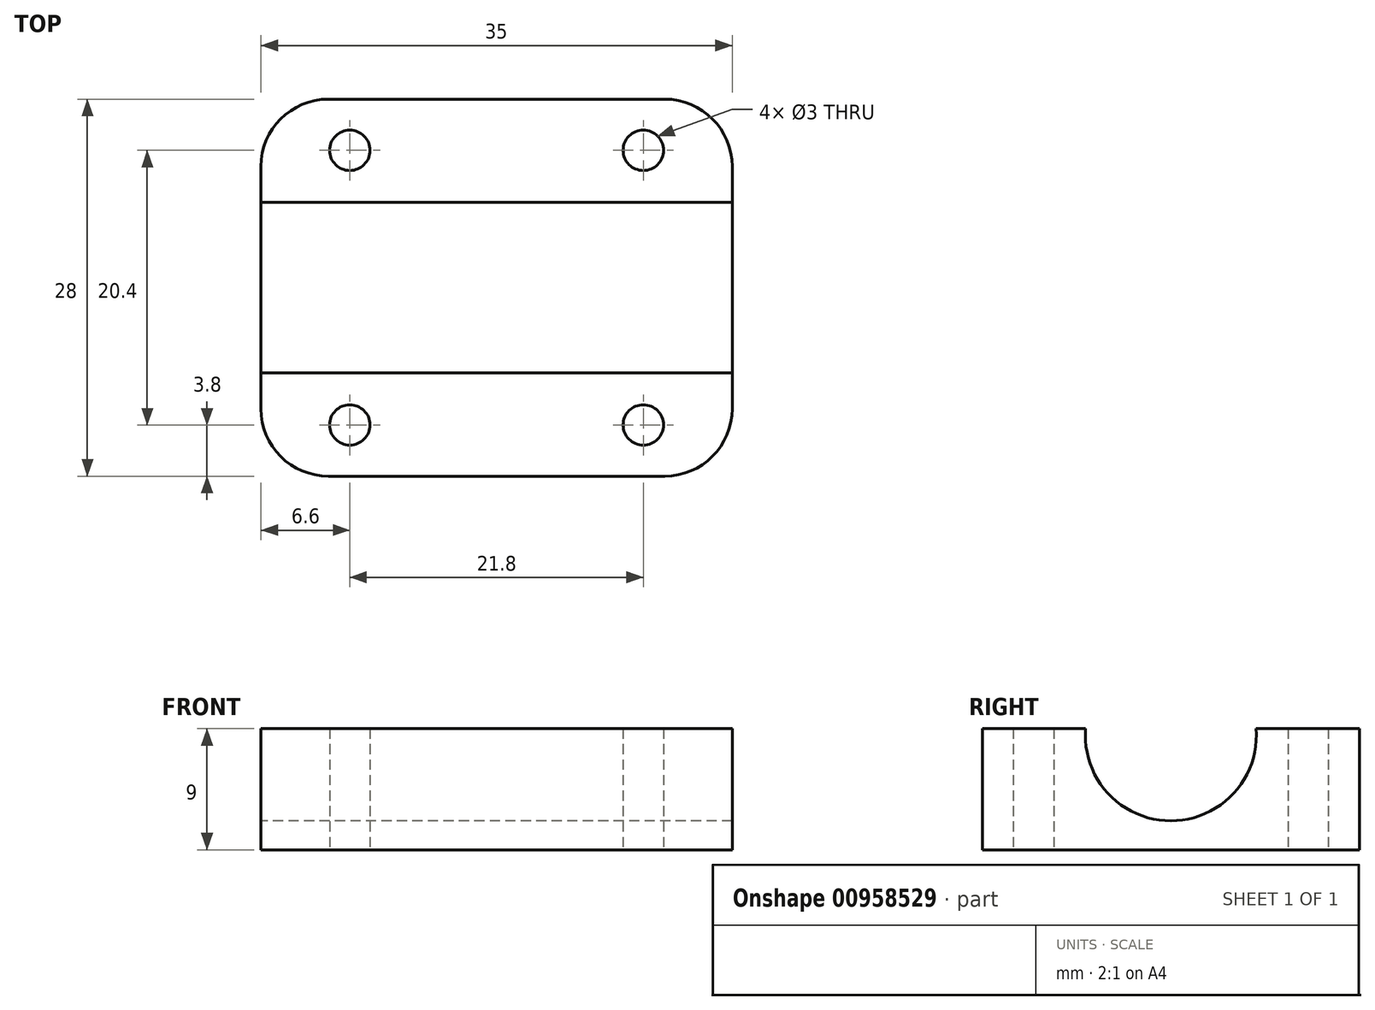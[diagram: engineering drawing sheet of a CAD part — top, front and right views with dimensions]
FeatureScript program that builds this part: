
annotation { "Feature Type Name" : "Feature", "Feature Type Description" : "" }
export const myFeature = defineFeature(function(context is Context, id is Id, definition is map)
    precondition{}
    {
        {
            var Q0;
            Q0=qCreatedBy(makeId("Top.planeOp"),FACE);
            var sketch = newSketch(context, id + "F0", { "sketchPlane" : qUnion([Q0])});
            skLineSegment(sketch, "E0.bottom", {"start": v(-17.5, 14) * mm, "end": v(17.5, 14) * mm});
            skLineSegment(sketch, "E0.top", {"start": v(-17.5, -14) * mm, "end": v(17.5, -14) * mm});
            skLineSegment(sketch, "E0.left", {"start": v(-17.5, 14) * mm, "end": v(-17.5, -14) * mm});
            skLineSegment(sketch, "E0.right", {"start": v(17.5, 14) * mm, "end": v(17.5, -14) * mm});
            skPoint(sketch, "E0.middle", {"position": v(0, 0) * mm});
            skPoint(sketch, "E1", {"position": v(-10.9, -10.2) * mm});
            skPoint(sketch, "E2.0.1.0", {"position": v(-10.9, 10.2) * mm});
            skPoint(sketch, "E2.1.0.0", {"position": v(10.9, -10.2) * mm});
            skPoint(sketch, "E2.1.1.0", {"position": v(10.9, 10.2) * mm});
            skLineSegment(sketch, "E2.direction1", {"start": v(-10.9, -10.2) * mm, "end": v(10.9, -10.2) * mm, "construction": true});
            skLineSegment(sketch, "E2.direction2", {"start": v(-10.9, -10.2) * mm, "end": v(-10.9, 10.2) * mm, "construction": true});
            skSolve(sketch);
        }
        {
            var Q0;
            Q0=makeQuery(id+"F0.imprint","IMPRINT",FACE,{"disambiguationData":[TD([[makeQuery(id+"F0.imprint","IMPRINT",EDGE,{"derivedFrom":sQuery(id+"F0.wireOp",EDGE,"E0.bottom")}),-1.0]])]});
            extrude(context, id + "F1", {"entities" : qUnion([Q0]), "depth" : 14 * mm, "offsetDistance" : 25 * mm});
        }
        {
            var Q0;
            Q0=makeQuery(id+"F1.opExtrude","SWEPT_FACE",FACE,{"disambiguationData":[OSD([sQuery(id+"F0.wireOp",EDGE,"E0.left")])]});
            var sketch = newSketch(context, id + "F2", { "sketchPlane" : qUnion([Q0])});
            skLineSegment(sketch, "E3", {"start": v(-14, 7) * mm, "end": v(14, 7) * mm});
            skPoint(sketch, "E4", {"position": v(0, 7) * mm});
            skSolve(sketch);
        }
        {
            var Q0;
            Q0=sQuery(id+"F2.wireOp",VERTEX,"E4");
            var Q1;
            Q1=makeQuery(id+"F1.opExtrude","SWEPT_BODY",BODY,{"disambiguationData":[OSD([sQuery(id+"F0.wireOp",EDGE,"E0.bottom"),sQuery(id+"F0.wireOp",EDGE,"E0.top"),sQuery(id+"F0.wireOp",EDGE,"E0.left"),sQuery(id+"F0.wireOp",EDGE,"E0.right")])]});
            hole(context, id + "F3", {"style" : HoleStyle.SIMPLE, "endStyle" : HoleEndStyle.THROUGH, "holeDiameter" : 12.7 * mm, "majorDiameter" : 5 * mm, "isTappedThrough" : true, "tappedDepth" : 12 * mm, "tapClearance" : 3, "startFromSketch" : true, "locations" : qUnion([Q0]), "scope" : qUnion([Q1])});
        }
        {
            var Q0;
            Q0=makeQuery(id+"F1.opExtrude","CAP_FACE",FACE,{"disambiguationData":[OSD([sQuery(id+"F0.wireOp",EDGE,"E0.bottom"),sQuery(id+"F0.wireOp",EDGE,"E0.top"),sQuery(id+"F0.wireOp",EDGE,"E0.left"),sQuery(id+"F0.wireOp",EDGE,"E0.right")])],"isStart":false});
            extrude(context, id + "F4", {"entities" : qUnion([Q0]), "operationType" : NewBodyOperationType.REMOVE, "oppositeDirection" : true, "depth" : 6.5 * mm, "offsetDistance" : 25 * mm});
        }
        {
            var Q0;
            Q0=sQuery(id+"F0.wireOp",VERTEX,"E2.1.1.0");
            var Q1;
            Q1=sQuery(id+"F0.wireOp",VERTEX,"E2.0.1.0");
            var Q2;
            Q2=sQuery(id+"F0.wireOp",VERTEX,"E1");
            var Q3;
            Q3=sQuery(id+"F0.wireOp",VERTEX,"E2.1.0.0");
            var Q4;
            Q4=makeQuery(id+"F1.opExtrude","SWEPT_BODY",BODY,{"disambiguationData":[OSD([sQuery(id+"F0.wireOp",EDGE,"E0.bottom"),sQuery(id+"F0.wireOp",EDGE,"E0.top"),sQuery(id+"F0.wireOp",EDGE,"E0.left"),sQuery(id+"F0.wireOp",EDGE,"E0.right")])]});
            hole(context, id + "F5", {"style" : HoleStyle.SIMPLE, "endStyle" : HoleEndStyle.THROUGH, "oppositeDirection" : true, "holeDiameter" : 3 * mm, "majorDiameter" : 5 * mm, "isTappedThrough" : true, "tappedDepth" : 12 * mm, "tapClearance" : 3, "startFromSketch" : true, "locations" : qUnion([Q0, Q1, Q2, Q3]), "scope" : qUnion([Q4])});
        }
        {
            var Q0;
            Q0=makeQuery(id+"F1.opExtrude","CAP_FACE",FACE,{"disambiguationData":[OSD([sQuery(id+"F0.wireOp",EDGE,"E0.bottom"),sQuery(id+"F0.wireOp",EDGE,"E0.top"),sQuery(id+"F0.wireOp",EDGE,"E0.left"),sQuery(id+"F0.wireOp",EDGE,"E0.right")])],"isStart":true});
            extrude(context, id + "F6", {"entities" : qUnion([Q0]), "operationType" : NewBodyOperationType.ADD, "depth" : 1.5 * mm, "offsetDistance" : 25 * mm});
        }
        {
            var Q0;
            {var subQ0=sQuery(id+"F0.wireOp",EDGE,"E0.left");var subQ1=sQuery(id+"F0.wireOp",EDGE,"E0.top");Q0=makeQuery(id+"F6.boolean.opBoolean","MERGE",EDGE,{"derivedFrom":[makeQuery(id+"F1.opExtrude","SWEPT_EDGE",EDGE,{"disambiguationData":[OSD([subQ1,subQ0])]}),makeQuery(id+"F6.opExtrude","SWEPT_EDGE",EDGE,{"disambiguationData":[OSD([subQ1,subQ0])]})]});}
            var Q1;
            {var subQ0=sQuery(id+"F0.wireOp",EDGE,"E0.left");var subQ1=sQuery(id+"F0.wireOp",EDGE,"E0.bottom");Q1=makeQuery(id+"F6.boolean.opBoolean","MERGE",EDGE,{"derivedFrom":[makeQuery(id+"F1.opExtrude","SWEPT_EDGE",EDGE,{"disambiguationData":[OSD([subQ1,subQ0])]}),makeQuery(id+"F6.opExtrude","SWEPT_EDGE",EDGE,{"disambiguationData":[OSD([subQ1,subQ0])]})]});}
            var Q2;
            {var subQ0=sQuery(id+"F0.wireOp",EDGE,"E0.right");var subQ1=sQuery(id+"F0.wireOp",EDGE,"E0.bottom");Q2=makeQuery(id+"F6.boolean.opBoolean","MERGE",EDGE,{"derivedFrom":[makeQuery(id+"F1.opExtrude","SWEPT_EDGE",EDGE,{"disambiguationData":[OSD([subQ1,subQ0])]}),makeQuery(id+"F6.opExtrude","SWEPT_EDGE",EDGE,{"disambiguationData":[OSD([subQ1,subQ0])]})]});}
            var Q3;
            {var subQ0=sQuery(id+"F0.wireOp",EDGE,"E0.right");var subQ1=sQuery(id+"F0.wireOp",EDGE,"E0.top");Q3=makeQuery(id+"F6.boolean.opBoolean","MERGE",EDGE,{"derivedFrom":[makeQuery(id+"F1.opExtrude","SWEPT_EDGE",EDGE,{"disambiguationData":[OSD([subQ1,subQ0])]}),makeQuery(id+"F6.opExtrude","SWEPT_EDGE",EDGE,{"disambiguationData":[OSD([subQ1,subQ0])]})]});}
            fillet(context, id + "F7", {"entities" : qUnion([Q0, Q1, Q2, Q3]), "radius" : 5 * mm, "tangentPropagation" : true, "allowEdgeOverflow" : false});
        }
    });
